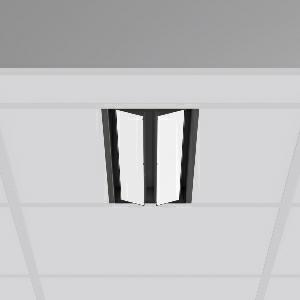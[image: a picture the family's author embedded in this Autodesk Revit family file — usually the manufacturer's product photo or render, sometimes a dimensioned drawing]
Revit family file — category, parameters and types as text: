
# Revit family: tx-move_901739_003_1_76_916b
name_source: partatom
category: Lighting Fixtures
units: mm (PartAtom-declared; Revit-internal decimal feet)

## family parameters
Cut with Voids When Loaded = No
Host = Face
Light Source = No
Part Type = Normal
Room Calculation Point = No
Round Connector Dimension = Use Diameter
Shared = No

## types (1)
- MultiLumen 1 (1 x LED Modul 840, 2450 lm, 4000)
    Apparent Load = 35 VA
    Approval mark = CE
    CIE Flux Codes = 47 79 96 100 100
    Color Rendering = 80
    Color Temperature = 4000
    Default Elevation = 1800 mm
    Description = Series: TX-MOVE
Einlege/Einbau-Flächenstrahler. Housing: sheet steel, powder-coated. 2xSwivel range: 90°. High-efficiency LED units with flush-mounted opal diffuser made of non-yellowing PMMA. Symmetrical wide beam light emission. Suitable for laying in grid ceiling module 625. Connected converter included in separate gearbox.Suitable for through-wiring.MultiLumen: Luminous flux adjustable in 3 steps. Accessories: Mounting frame for installation in suspended ceilings. Environmentally friendly and resource-saving due to replaceable and recyclable components. 
Colour: deep black, matt (RAL 9005)
Length: 622 mm
Width: 190 mm
Height: 39 mm
Cut-out length: 602 mm
Cut-out width: 174 mm
Recess height: 100 mm
Lamp: LED
Socket: without socket
Colour temperature: 4000K
Colour rendering index (CRI): 80
System power: 35 W
Rated luminous flux: 4900 lm
Luminous efficiency: 140 lm/W
System power 2: 47 W
Rated luminous flux 2: 6450 lm
Luminous efficiency 2: 137 lm/W
System power 3: 68 W
Rated luminous flux 3: 8750 lm
Luminous efficiency 3: 129 lm/W
Control gear: Dimmable EVG, DALI
Protection class: I
Type of protection: IP 20
    Height = 0 mm  [stored 0 ft]
    Lamp = 1 x LED Modul 840
    Lamp Light Flux = 2450 lm
    Lamp count = 1
    Length = 622 mm
    Lifetime = 50000 h
    Luminous efficacy = 140 lm/W
    Manufacturer = RZB
    ModVariant = No
    Model = 901739.003.1.76
    Mounting Place = Ceiling, Wall
    Mounting Type = Recessed
    Number of Poles = 1
    OnlyDefault = Yes
    Power Factor = 1
    Product Name = TX-MOVE
    Product group = Recessed projectors
    ProductGroupID = 401
    Protection Class = Protection class I
    Protection Degree = IP 20
    RLX_Detail_Level = 1
    RLX_Emergency_Light_Flux = 0 lm
    RLX_Emergency_Type = 0
    RLX_Emergency_Type_DB = No
    RlxData = <blob elided: 31549 chars, md5=b47ddd93>
    Socket = socket
    Standby Power = 0 W
    System Light Flux = 4900 lm
    System Power = 35 W
    Type Comments = MultiLumen 1
    Type Image = 901739.003.jpg
    URL = http://relux.com
    VarID = multilumen_1
    Voltage = 230 V
    Voltage Range = 220-240 V
    Weight = 0.00 kg
    Width = 190 mm  [stored 0.62336 ft]

note: [stored X ft] marks values corroborated as IEEE doubles in the binary element streams (Revit-internal decimal feet)

## geometry (parser evidence)
native form markers: Blend x4, Sweep x16
no freeform markers — native parametric forms only
